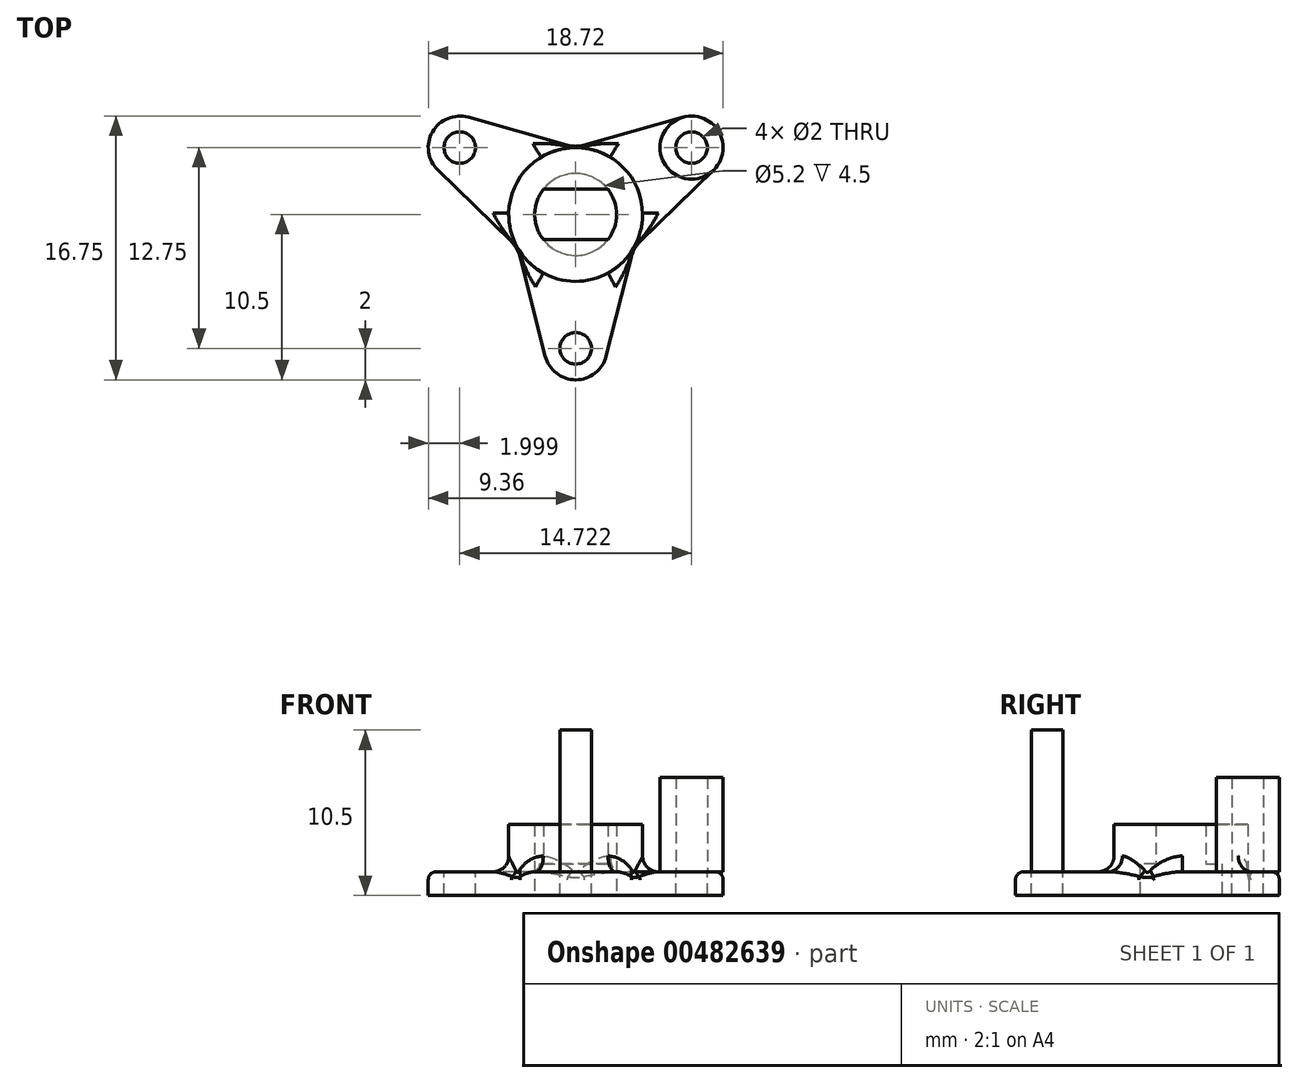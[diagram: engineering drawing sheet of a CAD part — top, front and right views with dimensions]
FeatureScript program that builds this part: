
annotation { "Feature Type Name" : "Feature", "Feature Type Description" : "" }
export const myFeature = defineFeature(function(context is Context, id is Id, definition is map)
    precondition{}
    {
        {
            var Q0;
            Q0=qCreatedBy(makeId("Top.planeOp"),FACE);
            var sketch = newSketch(context, id + "F0", { "sketchPlane" : qUnion([Q0])});
            skCircle(sketch, "E0.cCircle", {"center": v(0, 0) * mm, "radius": 4.25 * mm, "construction": true});
            skLineSegment(sketch, "E0.0", {"start": v(-7.36, 4.25) * mm, "end": v(7.36, 4.25) * mm});
            skLineSegment(sketch, "E0.1", {"start": v(7.36, 4.25) * mm, "end": v(0, -8.5) * mm});
            skLineSegment(sketch, "E0.2", {"start": v(0, -8.5) * mm, "end": v(-7.36, 4.25) * mm});
            skPoint(sketch, "E0.0.midPoint", {"position": v(0, 4.25) * mm});
            skCircle(sketch, "E1", {"center": v(-7.36, 4.25) * mm, "radius": 2.5 * mm, "construction": true});
            skCircle(sketch, "E2", {"center": v(7.36, 4.25) * mm, "radius": 2.5 * mm, "construction": true});
            skCircle(sketch, "E3", {"center": v(0, -8.5) * mm, "radius": 2.5 * mm, "construction": true});
            skCircle(sketch, "E4", {"center": v(0, 0) * mm, "radius": 11 * mm, "construction": true});
            skArc(sketch, "E5", {"start": v(-5.36, 4.25) * mm, "mid": v(-9.1, 5.25) * mm, "end": v(-6.36, 2.52) * mm});
            skArc(sketch, "E6", {"start": v(6.36, 2.52) * mm, "mid": v(9.1, 5.25) * mm, "end": v(5.36, 4.25) * mm});
            skArc(sketch, "E7", {"start": v(-1, -6.77) * mm, "mid": v(0, -10.5) * mm, "end": v(1, -6.77) * mm});
            skLineSegment(sketch, "E8", {"start": v(-3.68, -2.13) * mm, "end": v(-8.76, 2.82) * mm});
            skLineSegment(sketch, "E9", {"start": v(0, 4.25) * mm, "end": v(-6.82, 6.17) * mm});
            skLineSegment(sketch, "E10.1.0", {"start": v(-3.68, -2.12) * mm, "end": v(-1.94, -9) * mm});
            skLineSegment(sketch, "E10.1.1", {"start": v(3.68, -2.12) * mm, "end": v(1.94, -9) * mm});
            skLineSegment(sketch, "E10.2.0", {"start": v(3.68, -2.13) * mm, "end": v(8.76, 2.82) * mm});
            skLineSegment(sketch, "E10.2.1", {"start": v(0, 4.25) * mm, "end": v(6.82, 6.17) * mm});
            skSolve(sketch);
        }
        {
            var Q0;
            Q0=qSketchRegion(id+"F0",true);
            extrude(context, id + "F1", {"entities" : qUnion([Q0]), "depth" : 1.5 * mm});
        }
        {
            var Q0;
            Q0=makeQuery(id+"F1.opExtrude","CAP_FACE",FACE,{"disambiguationData":[OSD([sQuery(id+"F0.wireOp",EDGE,"E5"),sQuery(id+"F0.wireOp",EDGE,"E6"),sQuery(id+"F0.wireOp",EDGE,"E7"),sQuery(id+"F0.wireOp",EDGE,"E8"),sQuery(id+"F0.wireOp",EDGE,"E9"),sQuery(id+"F0.wireOp",EDGE,"E10.1.0"),sQuery(id+"F0.wireOp",EDGE,"E10.1.1"),sQuery(id+"F0.wireOp",EDGE,"E10.2.0"),sQuery(id+"F0.wireOp",EDGE,"E10.2.1")])],"isStart":true});
            var sketch = newSketch(context, id + "F2", { "sketchPlane" : qUnion([Q0])});
            skArc(sketch, "E11", {"start": v(-2.05, 1.6) * mm, "mid": v(-2.6, 0) * mm, "end": v(-2.05, -1.6) * mm});
            skLineSegment(sketch, "E12.rect.bottom", {"start": v(-2.05, 1.6) * mm, "end": v(2.05, 1.6) * mm});
            skLineSegment(sketch, "E12.rect.top", {"start": v(-2.05, -1.6) * mm, "end": v(2.05, -1.6) * mm});
            skLineSegment(sketch, "E12.rect.left", {"start": v(-2.05, 1.6) * mm, "end": v(-2.05, -1.6) * mm});
            skLineSegment(sketch, "E12.rect.right", {"start": v(2.05, 1.6) * mm, "end": v(2.05, -1.6) * mm});
            skArc(sketch, "E13.trimOffspring", {"start": v(2.05, -1.6) * mm, "mid": v(2.6, 0) * mm, "end": v(2.05, 1.6) * mm});
            skSolve(sketch);
        }
        {
            var Q0;
            Q0=qSketchRegion(id+"F2",true);
            extrude(context, id + "F3", {"entities" : qUnion([Q0]), "operationType" : NewBodyOperationType.REMOVE, "endBound" : BoundingType.THROUGH_ALL, "oppositeDirection" : true, "depth" : 25 * mm});
        }
        {
            var Q0;
            Q0=makeQuery(id+"F1.opExtrude","CAP_FACE",FACE,{"disambiguationData":[OSD([sQuery(id+"F0.wireOp",EDGE,"E5"),sQuery(id+"F0.wireOp",EDGE,"E6"),sQuery(id+"F0.wireOp",EDGE,"E7"),sQuery(id+"F0.wireOp",EDGE,"E8"),sQuery(id+"F0.wireOp",EDGE,"E9"),sQuery(id+"F0.wireOp",EDGE,"E10.1.0"),sQuery(id+"F0.wireOp",EDGE,"E10.1.1"),sQuery(id+"F0.wireOp",EDGE,"E10.2.0"),sQuery(id+"F0.wireOp",EDGE,"E10.2.1")])],"isStart":false});
            var sketch = newSketch(context, id + "F4", { "sketchPlane" : qUnion([Q0])});
            skCircle(sketch, "E14", {"center": v(0, 0) * mm, "radius": 4.25 * mm});
            skLineSegment(sketch, "E15.0", {"start": v(2.05, 1.6) * mm, "end": v(-2.05, 1.6) * mm});
            skArc(sketch, "E15.1", {"start": v(-2.05, 1.6) * mm, "mid": v(-2.6, 0) * mm, "end": v(-2.05, -1.6) * mm});
            skLineSegment(sketch, "E15.2", {"start": v(2.05, -1.6) * mm, "end": v(-2.05, -1.6) * mm});
            skArc(sketch, "E15.3", {"start": v(2.05, -1.6) * mm, "mid": v(2.6, 0) * mm, "end": v(2.05, 1.6) * mm});
            skSolve(sketch);
        }
        {
            var Q0;
            Q0=qSketchRegion(id+"F4",true);
            extrude(context, id + "F5", {"entities" : qUnion([Q0]), "operationType" : NewBodyOperationType.ADD, "depth" : 3 * mm});
        }
        {
            var Q0;
            {var subQ0=sQuery(id+"F0.wireOp",EDGE,"E5");var subQ1=sQuery(id+"F0.wireOp",EDGE,"E8");var subQ2=sQuery(id+"F0.wireOp",EDGE,"E9");var subQ3=sQuery(id+"F0.wireOp",EDGE,"E10.1.0");var subQ4=sQuery(id+"F0.wireOp",EDGE,"E10.2.1");var subQ5=makeQuery(id+"F1.opExtrude","CAP_FACE",FACE,{"disambiguationData":[OSD([subQ0,sQuery(id+"F0.wireOp",EDGE,"E6"),sQuery(id+"F0.wireOp",EDGE,"E7"),subQ1,subQ2,subQ3,sQuery(id+"F0.wireOp",EDGE,"E10.1.1"),sQuery(id+"F0.wireOp",EDGE,"E10.2.0"),subQ4])],"isStart":false});Q0=makeQuery(id+"F5.boolean.opBoolean","SPLIT",FACE,{"disambiguationData":[TD([makeQuery(id+"F1.opExtrude","SWEPT_FACE",FACE,{"disambiguationData":[OSD([subQ0])]})])],"derivedFrom":subQ5});}
            var sketch = newSketch(context, id + "F6", { "sketchPlane" : qUnion([Q0])});
            skCircle(sketch, "E16", {"center": v(-7.36, 4.25) * mm, "radius": 1 * mm});
            skCircle(sketch, "E17.1.0", {"center": v(0, -8.5) * mm, "radius": 1 * mm});
            skCircle(sketch, "E17.2.0", {"center": v(7.36, 4.25) * mm, "radius": 1 * mm});
            skPoint(sketch, "E17.center", {"position": v(0, 0) * mm});
            skSolve(sketch);
        }
        {
            var Q0;
            Q0=qSketchRegion(id+"F6",true);
            extrude(context, id + "F7", {"entities" : qUnion([Q0]), "operationType" : NewBodyOperationType.REMOVE, "endBound" : BoundingType.THROUGH_ALL, "oppositeDirection" : true, "depth" : 25 * mm});
        }
        {
            var Q0;
            {var subQ0=sQuery(id+"F0.wireOp",EDGE,"E7");var subQ1=sQuery(id+"F0.wireOp",EDGE,"E8");var subQ2=sQuery(id+"F0.wireOp",EDGE,"E10.1.0");var subQ3=sQuery(id+"F0.wireOp",EDGE,"E10.1.1");var subQ4=sQuery(id+"F0.wireOp",EDGE,"E10.2.0");var subQ5=makeQuery(id+"F1.opExtrude","CAP_FACE",FACE,{"disambiguationData":[OSD([sQuery(id+"F0.wireOp",EDGE,"E5"),sQuery(id+"F0.wireOp",EDGE,"E6"),subQ0,subQ1,sQuery(id+"F0.wireOp",EDGE,"E9"),subQ2,subQ3,subQ4,sQuery(id+"F0.wireOp",EDGE,"E10.2.1")])],"isStart":false});Q0=makeQuery(id+"F5.boolean.opBoolean","SPLIT",FACE,{"disambiguationData":[TD([makeQuery(id+"F1.opExtrude","SWEPT_FACE",FACE,{"disambiguationData":[OSD([subQ0])]})])],"derivedFrom":subQ5});}
            var sketch = newSketch(context, id + "F8", { "sketchPlane" : qUnion([Q0])});
            skCircle(sketch, "E18.0", {"center": v(0, -8.5) * mm, "radius": 1 * mm});
            skSolve(sketch);
        }
        {
            var Q0;
            Q0=qSketchRegion(id+"F8",true);
            extrude(context, id + "F9", {"entities" : qUnion([Q0]), "depth" : 9 * mm});
        }
        {
            var Q0;
            {var subQ0=sQuery(id+"F0.wireOp",EDGE,"E6");var subQ1=sQuery(id+"F0.wireOp",EDGE,"E9");var subQ2=sQuery(id+"F0.wireOp",EDGE,"E10.1.1");var subQ3=sQuery(id+"F0.wireOp",EDGE,"E10.2.0");var subQ4=sQuery(id+"F0.wireOp",EDGE,"E10.2.1");var subQ5=makeQuery(id+"F1.opExtrude","CAP_FACE",FACE,{"disambiguationData":[OSD([sQuery(id+"F0.wireOp",EDGE,"E5"),subQ0,sQuery(id+"F0.wireOp",EDGE,"E7"),sQuery(id+"F0.wireOp",EDGE,"E8"),subQ1,sQuery(id+"F0.wireOp",EDGE,"E10.1.0"),subQ2,subQ3,subQ4])],"isStart":false});Q0=makeQuery(id+"F5.boolean.opBoolean","SPLIT",FACE,{"disambiguationData":[TD([makeQuery(id+"F1.opExtrude","SWEPT_FACE",FACE,{"disambiguationData":[OSD([subQ0])]})])],"derivedFrom":subQ5});}
            var sketch = newSketch(context, id + "F10", { "sketchPlane" : qUnion([Q0])});
            skCircle(sketch, "E19.0", {"center": v(7.36, 4.25) * mm, "radius": 1 * mm});
            skCircle(sketch, "E20", {"center": v(7.36, 4.25) * mm, "radius": 2 * mm});
            skSolve(sketch);
        }
        {
            var Q0;
            Q0=qSketchRegion(id+"F10",true);
            extrude(context, id + "F11", {"entities" : qUnion([Q0]), "depth" : 6 * mm});
        }
        {
            var Q0;
            Q0=makeQuery(id+"F1.opExtrude","CAP_EDGE",EDGE,{"disambiguationData":[OSD([sQuery(id+"F0.wireOp",EDGE,"E10.1.1")])],"isStart":false});
            fillet(context, id + "F12", {"entities" : qUnion([Q0]), "radius" : 0.5 * mm, "tangentPropagation" : true, "allowEdgeOverflow" : false});
        }
        {
            var Q0;
            Q0=makeQuery(id+"F1.opExtrude","CAP_EDGE",EDGE,{"disambiguationData":[OSD([sQuery(id+"F0.wireOp",EDGE,"E10.2.0")])],"isStart":false});
            fillet(context, id + "F13", {"entities" : qUnion([Q0]), "radius" : 0.5 * mm, "tangentPropagation" : true, "allowEdgeOverflow" : false});
        }
        {
            var Q0;
            Q0=makeQuery(id+"F1.opExtrude","CAP_EDGE",EDGE,{"disambiguationData":[OSD([sQuery(id+"F0.wireOp",EDGE,"E9")])],"isStart":false});
            fillet(context, id + "F14", {"entities" : qUnion([Q0]), "radius" : 0.5 * mm, "tangentPropagation" : true, "allowEdgeOverflow" : false});
        }
        {
            var Q0;
            Q0=makeQuery(id+"F1.opExtrude","SWEPT_EDGE",EDGE,{"disambiguationData":[OSD([sQuery(id+"F0.wireOp",EDGE,"E0.0"),sQuery(id+"F0.wireOp",EDGE,"E9"),sQuery(id+"F0.wireOp",EDGE,"E10.2.1")])]});
            var Q1;
            Q1=makeQuery(id+"F1.opExtrude","SWEPT_EDGE",EDGE,{"disambiguationData":[OSD([sQuery(id+"F0.wireOp",EDGE,"E0.2"),sQuery(id+"F0.wireOp",EDGE,"E8"),sQuery(id+"F0.wireOp",EDGE,"E10.1.0")])]});
            var Q2;
            Q2=makeQuery(id+"F1.opExtrude","SWEPT_EDGE",EDGE,{"disambiguationData":[OSD([sQuery(id+"F0.wireOp",EDGE,"E0.1"),sQuery(id+"F0.wireOp",EDGE,"E10.1.1"),sQuery(id+"F0.wireOp",EDGE,"E10.2.0")])]});
            fillet(context, id + "F15", {"entities" : qUnion([Q0, Q1, Q2]), "radius" : 2 * mm, "tangentPropagation" : true, "allowEdgeOverflow" : false});
        }
        {
            var Q0;
            {var subQ0=sQuery(id+"F0.wireOp",EDGE,"E10.1.0");var subQ1=sQuery(id+"F0.wireOp",EDGE,"E9");var subQ2=sQuery(id+"F4.wireOp",EDGE,"E14");var subQ3=sQuery(id+"F0.wireOp",EDGE,"E8");var subQ4=sQuery(id+"F0.wireOp",EDGE,"E10.2.1");Q0=makeQuery(id+"F5.boolean.opBoolean","SPLIT",EDGE,{"disambiguationData":[TD([makeQuery(id+"F1.opExtrude","CAP_FACE",FACE,{"disambiguationData":[OSD([sQuery(id+"F0.wireOp",EDGE,"E5"),sQuery(id+"F0.wireOp",EDGE,"E6"),sQuery(id+"F0.wireOp",EDGE,"E7"),subQ3,subQ1,subQ0,sQuery(id+"F0.wireOp",EDGE,"E10.1.1"),sQuery(id+"F0.wireOp",EDGE,"E10.2.0"),subQ4])],"isStart":false}),makeQuery(id+"F1.opExtrude","SWEPT_FACE",FACE,{"disambiguationData":[OSD([subQ3])]}),makeQuery(id+"F1.opExtrude","SWEPT_FACE",FACE,{"disambiguationData":[OSD([subQ1])]}),makeQuery(id+"F1.opExtrude","SWEPT_FACE",FACE,{"disambiguationData":[OSD([subQ0])]}),makeQuery(id+"F1.opExtrude","SWEPT_FACE",FACE,{"disambiguationData":[OSD([subQ4])]}),makeQuery(id+"F5.opExtrude","SWEPT_FACE",FACE,{"disambiguationData":[OSD([subQ2])]})])],"derivedFrom":makeQuery(id+"F5.opExtrude","CAP_EDGE",EDGE,{"disambiguationData":[OSD([subQ2])],"isStart":true})});}
            fillet(context, id + "F16", {"entities" : qUnion([Q0]), "radius" : 1 * mm, "tangentPropagation" : true, "allowEdgeOverflow" : false});
        }
        {
            var Q0;
            Q0=makeQuery(id+"F1.opExtrude","CAP_FACE",FACE,{"disambiguationData":[OSD([sQuery(id+"F0.wireOp",EDGE,"E5"),sQuery(id+"F0.wireOp",EDGE,"E6"),sQuery(id+"F0.wireOp",EDGE,"E7"),sQuery(id+"F0.wireOp",EDGE,"E8"),sQuery(id+"F0.wireOp",EDGE,"E9"),sQuery(id+"F0.wireOp",EDGE,"E10.1.0"),sQuery(id+"F0.wireOp",EDGE,"E10.1.1"),sQuery(id+"F0.wireOp",EDGE,"E10.2.0"),sQuery(id+"F0.wireOp",EDGE,"E10.2.1")])],"isStart":true});
            var sketch = newSketch(context, id + "F17", { "sketchPlane" : qUnion([Q0])});
            skCircle(sketch, "E21", {"center": v(0, 0) * mm, "radius": 2.6 * mm});
            skSolve(sketch);
        }
        {
            var Q0;
            Q0=qSketchRegion(id+"F17",true);
            extrude(context, id + "F18", {"entities" : qUnion([Q0]), "operationType" : NewBodyOperationType.REMOVE, "oppositeDirection" : true, "depth" : 2 * mm});
        }
    });
